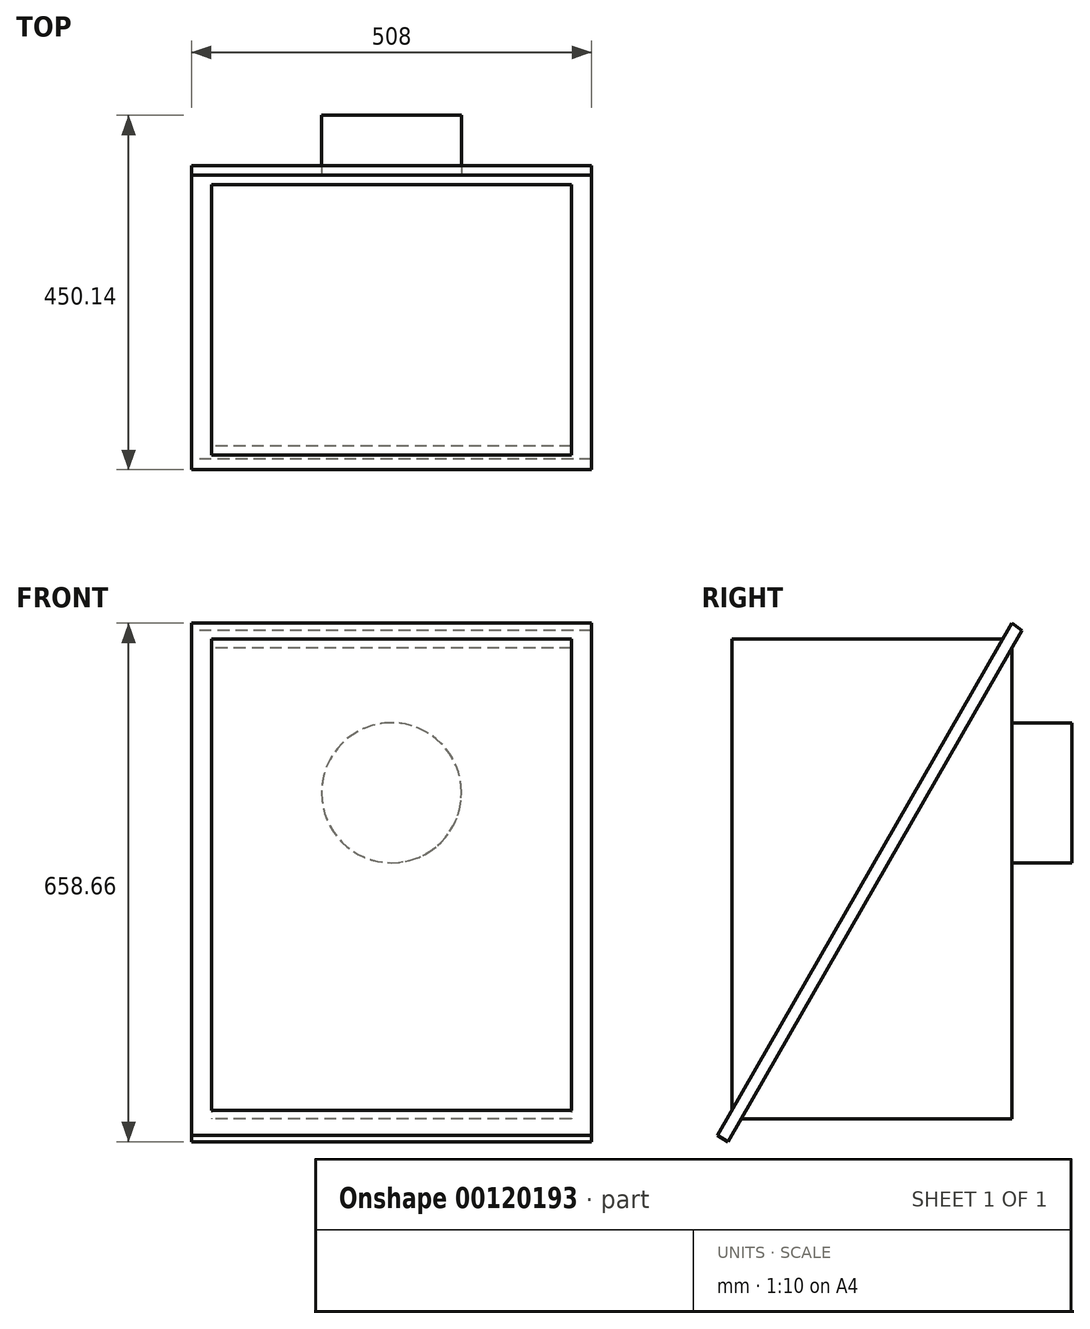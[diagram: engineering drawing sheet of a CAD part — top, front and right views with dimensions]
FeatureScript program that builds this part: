
annotation { "Feature Type Name" : "Feature", "Feature Type Description" : "" }
export const myFeature = defineFeature(function(context is Context, id is Id, definition is map)
    precondition{}
    {
        {
            var Q0;
            Q0=qCreatedBy(makeId("Front.planeOp"),FACE);
            var sketch = newSketch(context, id + "F0", { "sketchPlane" : qUnion([Q0])});
            skLineSegment(sketch, "E0.bottom", {"start": v(228.6, 304.8) * mm, "end": v(-228.6, 304.8) * mm});
            skLineSegment(sketch, "E0.top", {"start": v(228.6, -304.8) * mm, "end": v(-228.6, -304.8) * mm});
            skLineSegment(sketch, "E0.left", {"start": v(228.6, 304.8) * mm, "end": v(228.6, -304.8) * mm});
            skLineSegment(sketch, "E0.right", {"start": v(-228.6, 304.8) * mm, "end": v(-228.6, -304.8) * mm});
            skPoint(sketch, "E0.middle", {"position": v(0, 0) * mm});
            skSolve(sketch);
        }
        {
            var Q0;
            Q0 = qSketchRegion(id + "F0", true);
            extrude(context, id + "F1", {"entities" : qUnion([Q0]), "depth" : 355.6 * mm});
        }
        {
            var Q0;
            Q0=makeQuery(id+"F1.opExtrude","SWEPT_FACE",FACE,{"disambiguationData":[OSD([sQuery(id+"F0.wireOp",EDGE,"E0.right")])]});
            var sketch = newSketch(context, id + "F2", { "sketchPlane" : qUnion([Q0])});
            skLineSegment(sketch, "E1", {"start": v(0, 324.88) * mm, "end": v(373.94, -326) * mm});
            skLineSegment(sketch, "E2", {"start": v(373.94, -326) * mm, "end": v(360.4, -333.78) * mm});
            skLineSegment(sketch, "E3", {"start": v(360.4, -333.78) * mm, "end": v(-12.61, 315.48) * mm});
            skLineSegment(sketch, "E4", {"start": v(-12.61, 315.48) * mm, "end": v(0, 324.88) * mm});
            skSolve(sketch);
        }
        {
            var Q0;
            Q0 = qSketchRegion(id + "F2", true);
            extrude(context, id + "F3", {"entities" : qUnion([Q0]), "operationType" : NewBodyOperationType.ADD, "oppositeDirection" : true, "depth" : 482.6 * mm});
        }
        {
            var Q0;
            Q0=makeQuery(id+"F3.boolean.opBoolean","MERGE",FACE,{"derivedFrom":[makeQuery(id+"F1.opExtrude","SWEPT_FACE",FACE,{"disambiguationData":[OSD([sQuery(id+"F0.wireOp",EDGE,"E0.right")])]}),makeQuery(id+"F3.opExtrude","CAP_FACE",FACE,{"disambiguationData":[OSD([sQuery(id+"F2.wireOp",EDGE,"E1"),sQuery(id+"F2.wireOp",EDGE,"E2"),sQuery(id+"F2.wireOp",EDGE,"E3"),sQuery(id+"F2.wireOp",EDGE,"E4")])],"isStart":true})]});
            var sketch = newSketch(context, id + "F4", { "sketchPlane" : qUnion([Q0])});
            skLineSegment(sketch, "E5", {"start": v(0, 324.88) * mm, "end": v(373.94, -326) * mm});
            skLineSegment(sketch, "E6", {"start": v(373.94, -326) * mm, "end": v(360.4, -333.78) * mm});
            skLineSegment(sketch, "E7", {"start": v(360.4, -333.78) * mm, "end": v(-12.61, 315.48) * mm});
            skLineSegment(sketch, "E8", {"start": v(-12.61, 315.48) * mm, "end": v(0, 324.88) * mm});
            skSolve(sketch);
        }
        {
            var Q0;
            Q0 = qSketchRegion(id + "F4", true);
            extrude(context, id + "F5", {"entities" : qUnion([Q0]), "operationType" : NewBodyOperationType.ADD, "depth" : 25.4 * mm});
        }
        {
            var Q0;
            Q0=makeQuery(id+"F1.opExtrude","CAP_FACE",FACE,{"disambiguationData":[OSD([sQuery(id+"F0.wireOp",EDGE,"E0.bottom"),sQuery(id+"F0.wireOp",EDGE,"E0.top"),sQuery(id+"F0.wireOp",EDGE,"E0.left"),sQuery(id+"F0.wireOp",EDGE,"E0.right")])],"isStart":true});
            var sketch = newSketch(context, id + "F6", { "sketchPlane" : qUnion([Q0])});
            skCircle(sketch, "E9", {"center": v(0, 109.45) * mm, "radius": 88.9 * mm});
            skSolve(sketch);
        }
        {
            var Q0;
            Q0 = qSketchRegion(id + "F6", true);
            extrude(context, id + "F7", {"entities" : qUnion([Q0]), "operationType" : NewBodyOperationType.ADD, "depth" : 76.2 * mm});
        }
    });
